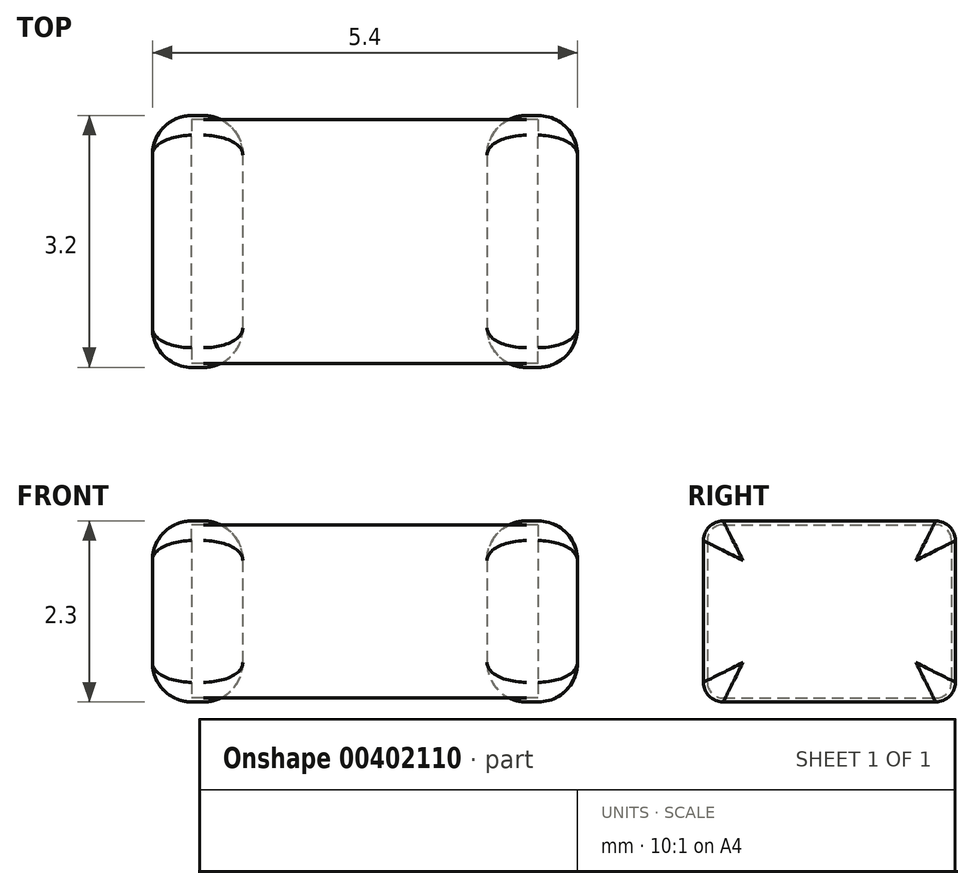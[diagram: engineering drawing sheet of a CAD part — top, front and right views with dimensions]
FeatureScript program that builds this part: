
annotation { "Feature Type Name" : "Feature", "Feature Type Description" : "" }
export const myFeature = defineFeature(function(context is Context, id is Id, definition is map)
    precondition{}
    {
        {
            var Q0;
            Q0=qCreatedBy(makeId("Top.planeOp"),FACE);
            var sketch = newSketch(context, id + "F0", { "sketchPlane" : qUnion([Q0])});
            skLineSegment(sketch, "E0.bottom", {"start": v(2.2, -1.55) * mm, "end": v(-2.2, -1.55) * mm});
            skLineSegment(sketch, "E0.top", {"start": v(2.2, 1.55) * mm, "end": v(-2.2, 1.55) * mm});
            skLineSegment(sketch, "E0.left", {"start": v(2.2, -1.55) * mm, "end": v(2.2, 1.55) * mm});
            skLineSegment(sketch, "E0.right", {"start": v(-2.2, -1.55) * mm, "end": v(-2.2, 1.55) * mm});
            skPoint(sketch, "E0.middle", {"position": v(0, 0) * mm});
            skSolve(sketch);
        }
        {
            var Q0;
            Q0 = qSketchRegion(id + "F0", true);
            extrude(context, id + "F1", {"entities" : qUnion([Q0]), "depth" : 2.2 * mm});
        }
        {
            var Q0;
            Q0=makeQuery(id+"F1.opExtrude","CAP_EDGE",EDGE,{"disambiguationData":[OSD([sQuery(id+"F0.wireOp",EDGE,"E0.bottom")])],"isStart":false});
            var Q1;
            Q1=makeQuery(id+"F1.opExtrude","CAP_EDGE",EDGE,{"disambiguationData":[OSD([sQuery(id+"F0.wireOp",EDGE,"E0.bottom")])],"isStart":true});
            var Q2;
            Q2=makeQuery(id+"F1.opExtrude","CAP_EDGE",EDGE,{"disambiguationData":[OSD([sQuery(id+"F0.wireOp",EDGE,"E0.top")])],"isStart":false});
            var Q3;
            Q3=makeQuery(id+"F1.opExtrude","CAP_EDGE",EDGE,{"disambiguationData":[OSD([sQuery(id+"F0.wireOp",EDGE,"E0.top")])],"isStart":true});
            fillet(context, id + "F2", {"entities" : qUnion([Q0, Q1, Q2, Q3]), "radius" : .2 * mm, "tangentPropagation" : true, "allowEdgeOverflow" : false});
        }
        {
            var Q0;
            Q0=makeQuery(id+"F1.opExtrude","SWEPT_FACE",FACE,{"disambiguationData":[OSD([sQuery(id+"F0.wireOp",EDGE,"E0.left")])]});
            var sketch = newSketch(context, id + "F3", { "sketchPlane" : qUnion([Q0])});
            skLineSegment(sketch, "E1.1.0", {"start": v(1.55, 2) * mm, "end": v(1.55, 0.2) * mm});
            skArc(sketch, "E1.1.1", {"start": v(1.55, 0.2) * mm, "mid": v(1.5, 0.06) * mm, "end": v(1.35, 0) * mm});
            skLineSegment(sketch, "E1.1.2", {"start": v(1.35, 0) * mm, "end": v(-1.35, 0) * mm});
            skArc(sketch, "E1.1.3", {"start": v(-1.35, 0) * mm, "mid": v(-1.5, 0.06) * mm, "end": v(-1.55, 0.2) * mm});
            skLineSegment(sketch, "E1.1.4", {"start": v(-1.55, 0.2) * mm, "end": v(-1.55, 2) * mm});
            skArc(sketch, "E1.1.5", {"start": v(-1.55, 2) * mm, "mid": v(-1.5, 2.14) * mm, "end": v(-1.35, 2.2) * mm});
            skLineSegment(sketch, "E1.1.6", {"start": v(-1.35, 2.2) * mm, "end": v(1.35, 2.2) * mm});
            skArc(sketch, "E1.1.7", {"start": v(1.35, 2.2) * mm, "mid": v(1.5, 2.14) * mm, "end": v(1.55, 2) * mm});
            skArc(sketch, "E2.0", {"start": v(-1.6, 0.2) * mm, "mid": v(-1.53, 0.02) * mm, "end": v(-1.35, -0.05) * mm});
            skLineSegment(sketch, "E2.1", {"start": v(-1.6, 2) * mm, "end": v(-1.6, 0.2) * mm});
            skLineSegment(sketch, "E2.2", {"start": v(-1.35, -0.05) * mm, "end": v(1.35, -0.05) * mm});
            skArc(sketch, "E2.3", {"start": v(-1.35, 2.25) * mm, "mid": v(-1.53, 2.18) * mm, "end": v(-1.6, 2) * mm});
            skArc(sketch, "E2.4", {"start": v(1.35, -0.05) * mm, "mid": v(1.53, 0.02) * mm, "end": v(1.6, 0.2) * mm});
            skLineSegment(sketch, "E2.5", {"start": v(1.6, 0.2) * mm, "end": v(1.6, 2) * mm});
            skArc(sketch, "E2.6", {"start": v(1.6, 2) * mm, "mid": v(1.53, 2.18) * mm, "end": v(1.35, 2.25) * mm});
            skLineSegment(sketch, "E2.7", {"start": v(1.35, 2.25) * mm, "end": v(-1.35, 2.25) * mm});
            skSolve(sketch);
        }
        {
            var Q0;
            Q0=makeQuery(id+"F3.imprint","IMPRINT",FACE,{"disambiguationData":[TD([[makeQuery(id+"F3.imprint","IMPRINT",EDGE,{"derivedFrom":sQuery(id+"F3.wireOp",EDGE,"E1.1.0")}),1.0]])]});
            var Q1;
            Q1=makeQuery(id+"F3.imprint","IMPRINT",FACE,{"disambiguationData":[TD([[makeQuery(id+"F3.imprint","IMPRINT",EDGE,{"derivedFrom":sQuery(id+"F3.wireOp",EDGE,"E1.1.0")}),-1.0]])]});
            extrude(context, id + "F4", {"entities" : qUnion([Q0, Q1]), "depth" : .5 * mm, "hasSecondDirection" : true, "secondDirectionOppositeDirection" : true, "secondDirectionDepth" : .65 * mm});
        }
        {
            var Q0;
            Q0=makeQuery(id+"F4.opExtrude","SWEPT_BODY",BODY,{"disambiguationData":[OSD([sQuery(id+"F3.wireOp",EDGE,"E2.0"),sQuery(id+"F3.wireOp",EDGE,"E2.1"),sQuery(id+"F3.wireOp",EDGE,"E2.2"),sQuery(id+"F3.wireOp",EDGE,"E2.3"),sQuery(id+"F3.wireOp",EDGE,"E2.4"),sQuery(id+"F3.wireOp",EDGE,"E2.5"),sQuery(id+"F3.wireOp",EDGE,"E2.6"),sQuery(id+"F3.wireOp",EDGE,"E2.7")])]});
            var Q1;
            Q1=qCreatedBy(makeId("Right.planeOp"),FACE);
            mirror(context, id + "F5", {"entities" : qUnion([Q0]), "mirrorPlane" : qUnion([Q1])});
        }
        {
            var Q0;
            Q0=makeQuery(id+"F5.opPattern","COPY",EDGE,{"derivedFrom":makeQuery(id+"F4.opExtrude","CAP_EDGE",EDGE,{"disambiguationData":[OSD([sQuery(id+"F3.wireOp",EDGE,"E2.7")])],"isStart":true}),"instanceName":"1"});
            var Q1;
            Q1=makeQuery(id+"F5.opPattern","COPY",FACE,{"derivedFrom":makeQuery(id+"F4.opExtrude","CAP_FACE",FACE,{"disambiguationData":[OSD([sQuery(id+"F3.wireOp",EDGE,"E2.0"),sQuery(id+"F3.wireOp",EDGE,"E2.1"),sQuery(id+"F3.wireOp",EDGE,"E2.2"),sQuery(id+"F3.wireOp",EDGE,"E2.3"),sQuery(id+"F3.wireOp",EDGE,"E2.4"),sQuery(id+"F3.wireOp",EDGE,"E2.5"),sQuery(id+"F3.wireOp",EDGE,"E2.6"),sQuery(id+"F3.wireOp",EDGE,"E2.7")])],"isStart":false}),"instanceName":"1"});
            var Q2;
            Q2=makeQuery(id+"F4.opExtrude","CAP_FACE",FACE,{"disambiguationData":[OSD([sQuery(id+"F3.wireOp",EDGE,"E2.0"),sQuery(id+"F3.wireOp",EDGE,"E2.1"),sQuery(id+"F3.wireOp",EDGE,"E2.2"),sQuery(id+"F3.wireOp",EDGE,"E2.3"),sQuery(id+"F3.wireOp",EDGE,"E2.4"),sQuery(id+"F3.wireOp",EDGE,"E2.5"),sQuery(id+"F3.wireOp",EDGE,"E2.6"),sQuery(id+"F3.wireOp",EDGE,"E2.7")])],"isStart":false});
            var Q3;
            Q3=makeQuery(id+"F4.opExtrude","CAP_EDGE",EDGE,{"disambiguationData":[OSD([sQuery(id+"F3.wireOp",EDGE,"E2.1")])],"isStart":true});
            fillet(context, id + "F6", {"entities" : qUnion([Q0, Q1, Q2, Q3]), "radius" : .5 * mm, "tangentPropagation" : true, "allowEdgeOverflow" : false});
        }
    });
